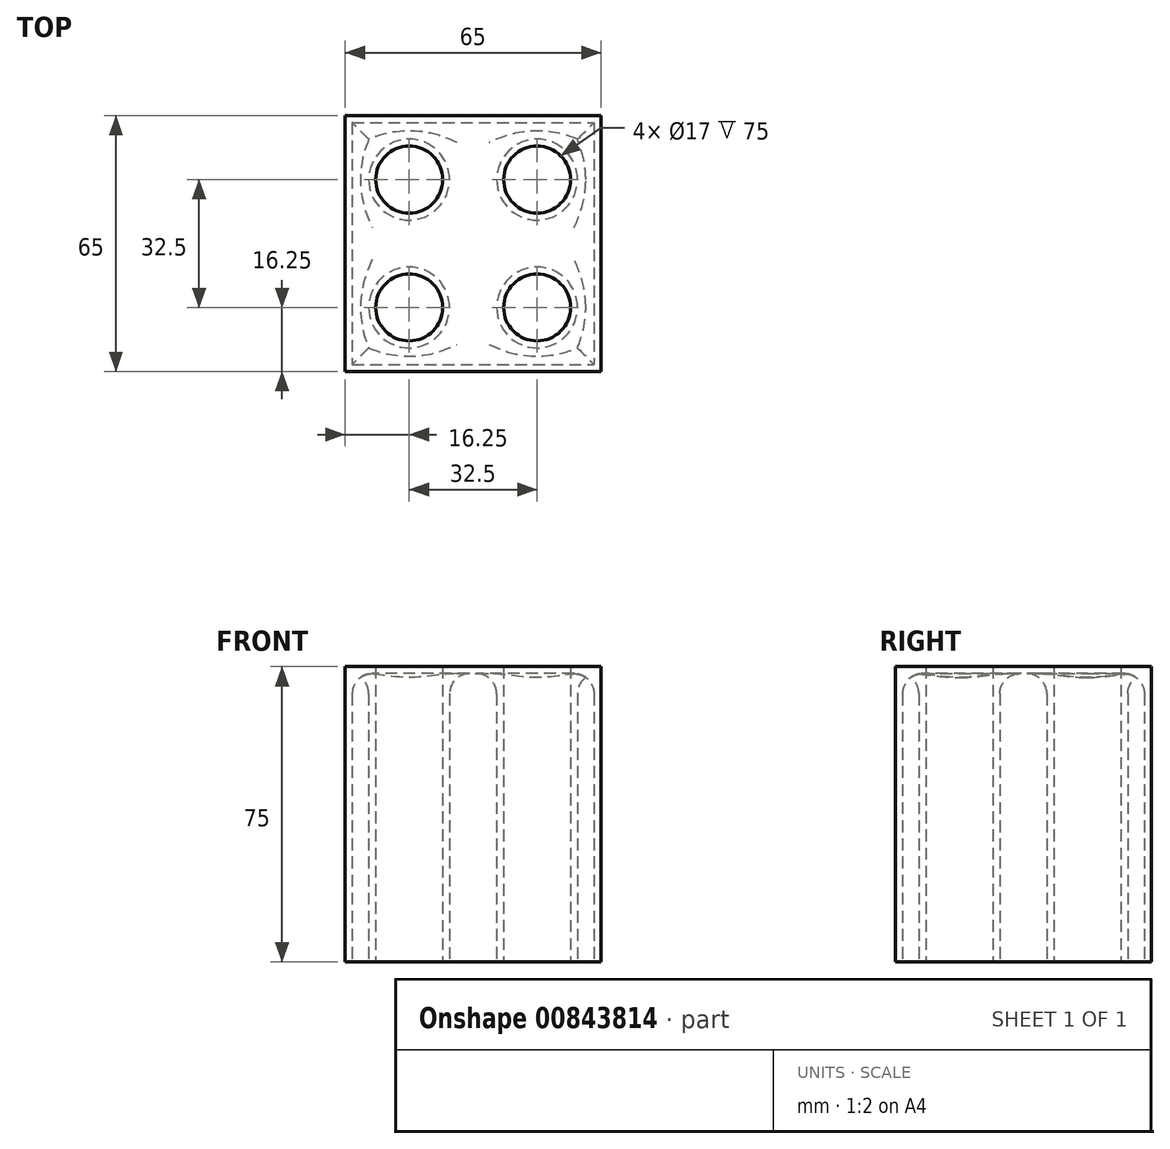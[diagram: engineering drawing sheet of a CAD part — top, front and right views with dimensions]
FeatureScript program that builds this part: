
annotation { "Feature Type Name" : "Feature", "Feature Type Description" : "" }
export const myFeature = defineFeature(function(context is Context, id is Id, definition is map)
    precondition{}
    {
        {
            var Q0;
            Q0=qCreatedBy(makeId("Top.planeOp"),FACE);
            var sketch = newSketch(context, id + "F0", { "sketchPlane" : qUnion([Q0])});
            skPoint(sketch, "E0.middle", {"position": v(0, 0) * mm});
            skLineSegment(sketch, "E1.bottom", {"start": v(-34, 34) * mm, "end": v(34, 34) * mm});
            skLineSegment(sketch, "E1.top", {"start": v(-34, -34) * mm, "end": v(34, -34) * mm});
            skLineSegment(sketch, "E1.left", {"start": v(-34, 34) * mm, "end": v(-34, -34) * mm});
            skLineSegment(sketch, "E1.right", {"start": v(34, 34) * mm, "end": v(34, -34) * mm});
            skLineSegment(sketch, "E2.bottom", {"start": v(-32.5, 32.5) * mm, "end": v(32.5, 32.5) * mm});
            skLineSegment(sketch, "E2.top", {"start": v(-32.5, -32.5) * mm, "end": v(32.5, -32.5) * mm});
            skLineSegment(sketch, "E2.left", {"start": v(-32.5, 32.5) * mm, "end": v(-32.5, -32.5) * mm});
            skLineSegment(sketch, "E2.right", {"start": v(32.5, 32.5) * mm, "end": v(32.5, -32.5) * mm});
            skPoint(sketch, "E0.top.end.orphan", {"position": v(35, -35) * mm});
            skPoint(sketch, "E0.top.start.orphan", {"position": v(-35, -35) * mm});
            skPoint(sketch, "E0.bottom.end.orphan", {"position": v(35, 35) * mm});
            skPoint(sketch, "E0.bottom.start.orphan", {"position": v(-35, 35) * mm});
            skCircle(sketch, "E3", {"center": v(16.25, 16.25) * mm, "radius": 8.5 * mm});
            skCircle(sketch, "E4", {"center": v(16.25, -16.25) * mm, "radius": 8.5 * mm});
            skCircle(sketch, "E5", {"center": v(-16.25, 16.25) * mm, "radius": 8.5 * mm});
            skCircle(sketch, "E6", {"center": v(-16.25, -16.25) * mm, "radius": 8.5 * mm});
            skSolve(sketch);
        }
        {
            var Q0;
            Q0=makeQuery(id+"F0.imprint","IMPRINT",FACE,{"disambiguationData":[TD([[makeQuery(id+"F0.imprint","IMPRINT",EDGE,{"derivedFrom":sQuery(id+"F0.wireOp",EDGE,"E2.bottom")}),-1.0]])]});
            extrude(context, id + "F1", {"entities" : qUnion([Q0]), "depth" : 75 * mm, "offsetDistance" : 25.4 * mm});
        }
        {
            var Q0;
            Q0=makeQuery(id+"F1.opExtrude","CAP_FACE",FACE,{"disambiguationData":[OSD([sQuery(id+"F0.wireOp",EDGE,"E2.bottom"),sQuery(id+"F0.wireOp",EDGE,"E2.top"),sQuery(id+"F0.wireOp",EDGE,"E2.left"),sQuery(id+"F0.wireOp",EDGE,"E2.right"),sQuery(id+"F0.wireOp",EDGE,"E3"),sQuery(id+"F0.wireOp",EDGE,"E4"),sQuery(id+"F0.wireOp",EDGE,"E5"),sQuery(id+"F0.wireOp",EDGE,"E6")])],"isStart":true});
            shell(context, id + "F2", {"entities" : qUnion([Q0]), "thickness" : 1.78 * mm});
        }
        {
            var Q0;
            {var subQ0=sQuery(id+"F0.wireOp",EDGE,"E6");var subQ1=sQuery(id+"F0.wireOp",EDGE,"E5");var subQ2=sQuery(id+"F0.wireOp",EDGE,"E4");var subQ3=sQuery(id+"F0.wireOp",EDGE,"E3");var subQ4=sQuery(id+"F0.wireOp",EDGE,"E2.right");var subQ5=sQuery(id+"F0.wireOp",EDGE,"E2.left");var subQ6=sQuery(id+"F0.wireOp",EDGE,"E2.top");var subQ7=sQuery(id+"F0.wireOp",EDGE,"E2.bottom");Q0=makeQuery(id+"F2.opShell","OFFSET_FACE",FACE,{"disambiguationData":[OSD([subQ7,subQ6,subQ5,subQ4,subQ3,subQ2,subQ1,subQ0]),TDD([makeQuery(id+"F1.opExtrude","CAP_FACE",FACE,{"disambiguationData":[OSD([subQ7,subQ6,subQ5,subQ4,subQ3,subQ2,subQ1,subQ0])],"isStart":false})])]});}
            fillet(context, id + "F3", {"entities" : qUnion([Q0]), "radius" : 5.08 * mm, "tangentPropagation" : true, "allowEdgeOverflow" : false});
        }
    });
